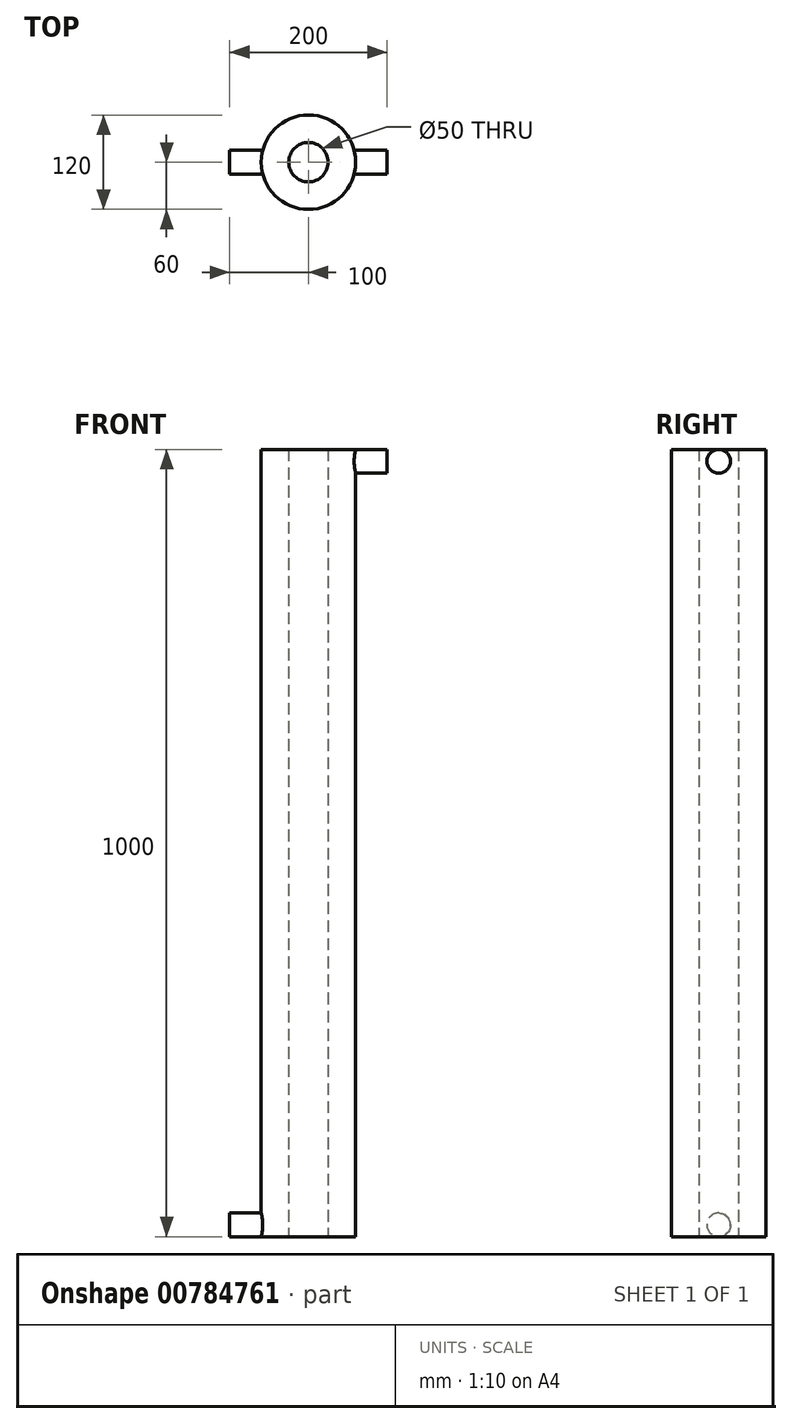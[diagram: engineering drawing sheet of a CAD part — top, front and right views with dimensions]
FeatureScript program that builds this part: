
annotation { "Feature Type Name" : "Feature", "Feature Type Description" : "" }
export const myFeature = defineFeature(function(context is Context, id is Id, definition is map)
    precondition{}
    {
        {
            var Q0;
            Q0=qCreatedBy(makeId("Top.planeOp"),FACE);
            var sketch = newSketch(context, id + "F0", { "sketchPlane" : qUnion([Q0])});
            skCircle(sketch, "E0", {"center": v(0, 0) * mm, "radius": 25 * mm});
            skCircle(sketch, "E1", {"center": v(0, 0) * mm, "radius": 60 * mm});
            skSolve(sketch);
        }
        {
            var Q0;
            Q0=qSketchRegion(id+"F0",true);
            extrude(context, id + "F1", {"entities" : qUnion([Q0]), "depth" : 1000 * mm, "offsetDistance" : 25.4 * mm, "symmetric" : true});
        }
        {
            var Q0;
            Q0=qCreatedBy(makeId("Right.planeOp"),FACE);
            var sketch = newSketch(context, id + "F2", { "sketchPlane" : qUnion([Q0])});
            skCircle(sketch, "E2", {"center": v(0, 485) * mm, "radius": 15 * mm});
            skSolve(sketch);
        }
        {
            var Q0;
            Q0=qSketchRegion(id+"F2",true);
            var Q1;
            Q1=makeQuery(id+"F1.opExtrude","SWEPT_FACE",FACE,{"disambiguationData":[OSD([sQuery(id+"F0.wireOp",EDGE,"E1")])]});
            extrude(context, id + "F3", {"entities" : qUnion([Q0]), "operationType" : NewBodyOperationType.ADD, "depth" : 100 * mm, "offsetDistance" : 25 * mm, "hasSecondDirection" : true, "secondDirectionBound" : BoundingType.UP_TO_SURFACE, "secondDirectionOppositeDirection" : false, "secondDirectionDepth" : 25 * mm, "secondDirectionBoundEntityFace" : qUnion([Q1]), "hasSecondDirectionOffset" : true, "secondDirectionOffsetDistance" : 0 * mm});
        }
        {
            var Q0;
            Q0=qCreatedBy(makeId("Right.planeOp"),FACE);
            var sketch = newSketch(context, id + "F4", { "sketchPlane" : qUnion([Q0])});
            skCircle(sketch, "E3", {"center": v(0, -485) * mm, "radius": 15 * mm});
            skSolve(sketch);
        }
        {
            var Q0;
            Q0=qSketchRegion(id+"F4",true);
            var Q1;
            Q1=makeQuery(id+"F1.opExtrude","SWEPT_FACE",FACE,{"disambiguationData":[OSD([sQuery(id+"F0.wireOp",EDGE,"E1")])]});
            extrude(context, id + "F5", {"entities" : qUnion([Q0]), "operationType" : NewBodyOperationType.ADD, "oppositeDirection" : true, "depth" : 100 * mm, "offsetDistance" : 25 * mm, "hasSecondDirection" : true, "secondDirectionBound" : BoundingType.UP_TO_SURFACE, "secondDirectionOppositeDirection" : true, "secondDirectionDepth" : 25 * mm, "secondDirectionBoundEntityFace" : qUnion([Q1]), "hasSecondDirectionOffset" : true, "secondDirectionOffsetDistance" : 0 * mm});
        }
    });
